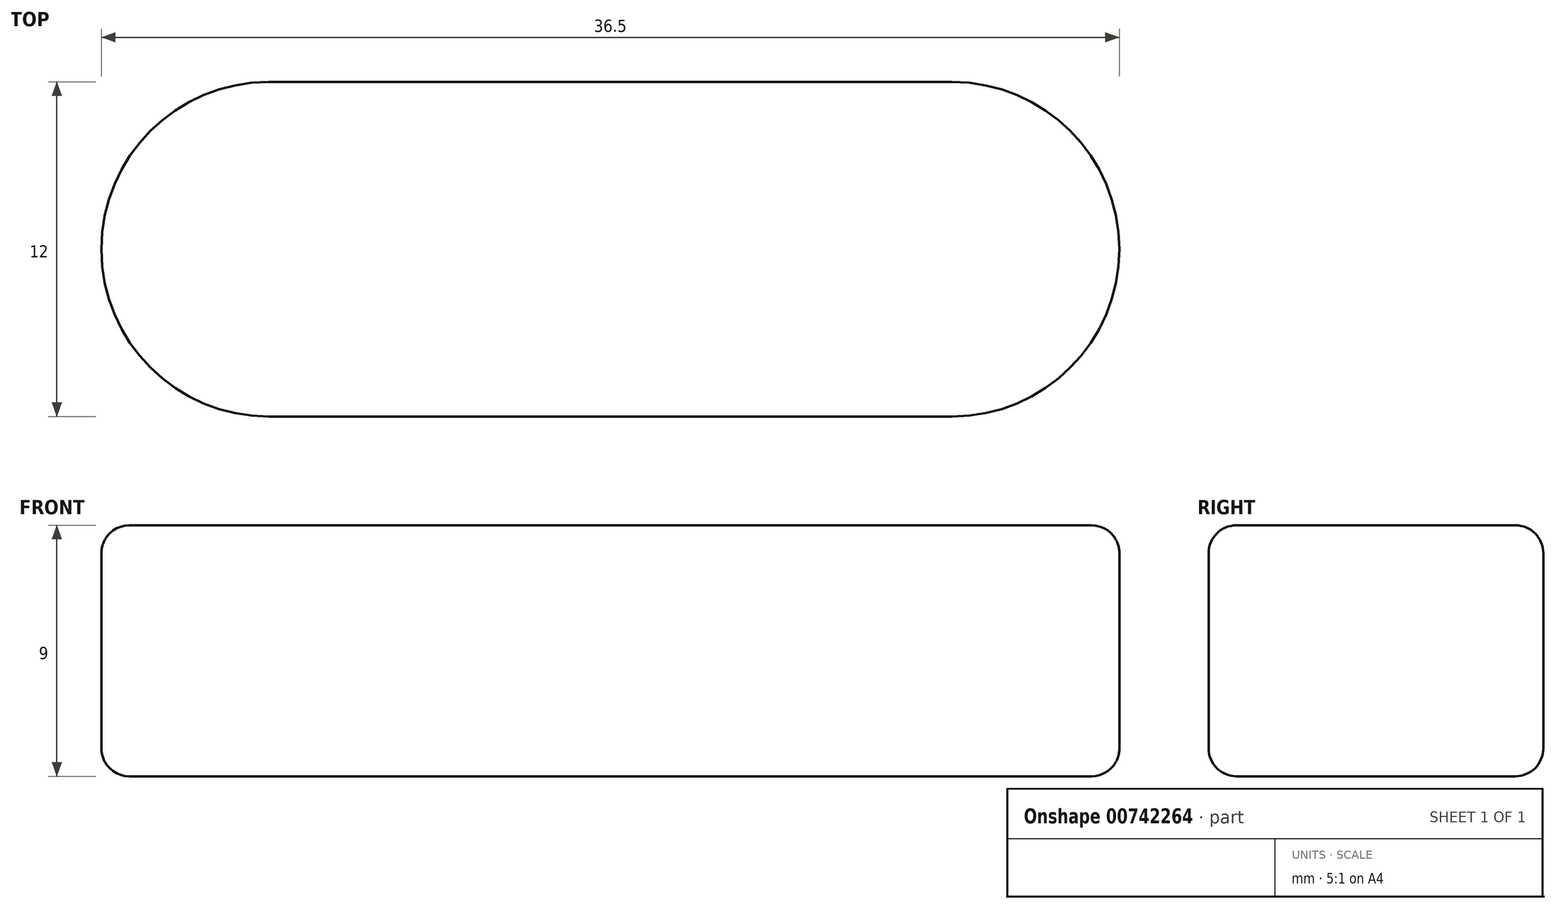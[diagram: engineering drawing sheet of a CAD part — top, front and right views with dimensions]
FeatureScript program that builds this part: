
annotation { "Feature Type Name" : "Feature", "Feature Type Description" : "" }
export const myFeature = defineFeature(function(context is Context, id is Id, definition is map)
    precondition{}
    {
        {
            var Q0;
            Q0=qCreatedBy(makeId("Top.planeOp"),FACE);
            var sketch = newSketch(context, id + "F0", { "sketchPlane" : qUnion([Q0])});
            skLineSegment(sketch, "E0.bottom", {"start": v(12.25, -6) * mm, "end": v(-12.25, -6) * mm});
            skLineSegment(sketch, "E0.top", {"start": v(12.25, 6) * mm, "end": v(-12.25, 6) * mm});
            skLineSegment(sketch, "E0.left", {"start": v(12.25, -6) * mm, "end": v(12.25, 6) * mm, "construction": true});
            skLineSegment(sketch, "E0.right", {"start": v(-12.25, -6) * mm, "end": v(-12.25, 6) * mm, "construction": true});
            skPoint(sketch, "E0.middle", {"position": v(0, 0) * mm});
            skArc(sketch, "E1", {"start": v(-12.25, 6) * mm, "mid": v(-18.25, 0) * mm, "end": v(-12.25, -6) * mm});
            skArc(sketch, "E2", {"start": v(12.25, -6) * mm, "mid": v(18.25, 0) * mm, "end": v(12.25, 6) * mm});
            skLineSegment(sketch, "E3", {"start": v(-18.25, 0) * mm, "end": v(-18.25, -5.01) * mm, "construction": true});
            skLineSegment(sketch, "E4", {"start": v(18.25, 0) * mm, "end": v(18.25, -4.93) * mm, "construction": true});
            skSolve(sketch);
        }
        {
            var Q0;
            Q0=makeQuery(id+"F0.imprint","IMPRINT",FACE,{"disambiguationData":[TD([[makeQuery(id+"F0.imprint","IMPRINT",EDGE,{"derivedFrom":sQuery(id+"F0.wireOp",EDGE,"E0.bottom")}),-1.0]])]});
            extrude(context, id + "F1", {"entities" : qUnion([Q0]), "depth" : 9 * mm, "offsetDistance" : 25 * mm});
        }
        {
            var Q0;
            Q0=makeQuery(id+"F1.opExtrude","CAP_EDGE",EDGE,{"disambiguationData":[OSD([sQuery(id+"F0.wireOp",EDGE,"E0.top")])],"isStart":true});
            var Q1;
            Q1=makeQuery(id+"F1.opExtrude","CAP_EDGE",EDGE,{"disambiguationData":[OSD([sQuery(id+"F0.wireOp",EDGE,"E0.top")])],"isStart":false});
            fillet(context, id + "F2", {"entities" : qUnion([Q0, Q1]), "radius" : 1 * mm, "tangentPropagation" : true, "allowEdgeOverflow" : false});
        }
    });
